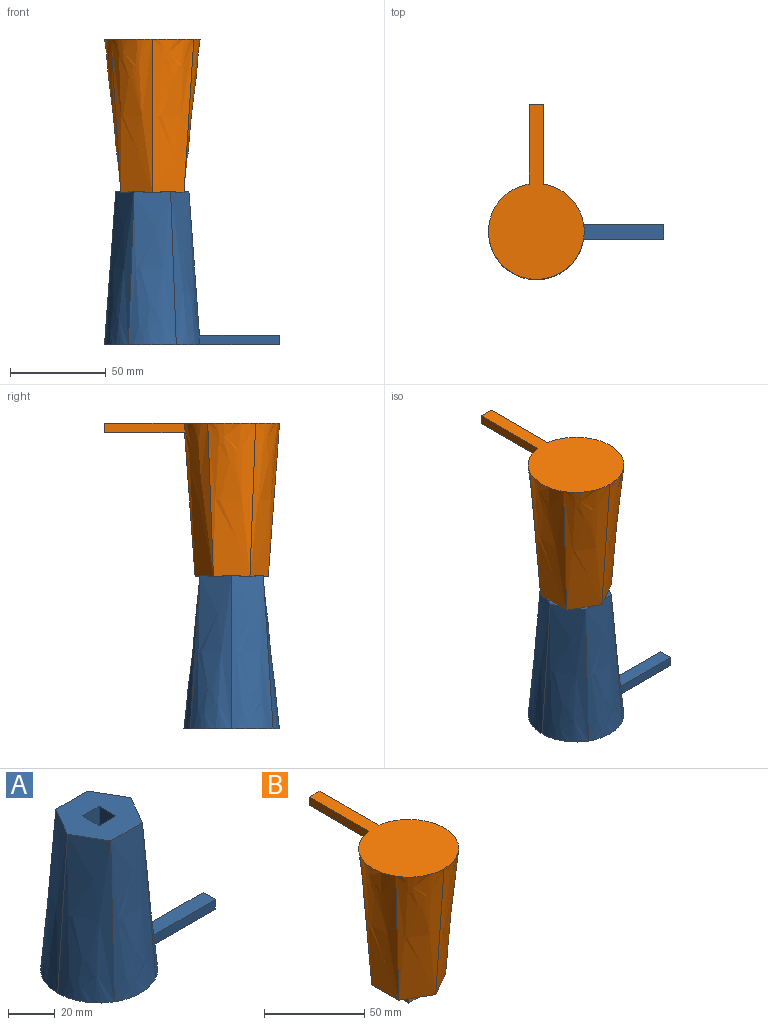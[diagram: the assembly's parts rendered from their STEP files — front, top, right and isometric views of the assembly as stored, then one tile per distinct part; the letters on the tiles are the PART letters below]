
ASSEMBLY  parts=2 mates=1
PART A: 19 faces, bbox 91.5x50x80 mm
  f0: bspline ~80x21.65mm, area 1787.3mm2, adj f1,f2,f6,f7,f16,f18
  f1: plane 91.45x50mm, normal (0,0,-1), area 1957.7mm2, adj f0,f3,f4,f5,f6,f7,f8,f15
  f2: plane 38.21x33.09mm, normal (0,0,1), area 846.4mm2, adj f0,f3,f4,f5,f6,f7,f10,f11
  f3: bspline ~80x25mm, area 1806mm2, adj f1,f2,f4,f7
  f4: bspline ~80x21.65mm, area 1806mm2, adj f1,f2,f3,f5
  f5: bspline ~80x21.65mm, area 1806mm2, adj f1,f2,f4,f6
  f6: bspline ~80x25mm, area 1806mm2, adj f0,f1,f2,f5
  f7: bspline ~80x21.65mm, area 1787.3mm2, adj f0,f1,f2,f3,f15,f18
  f8: cylinder r=10mm len=20mm, axis (0,0,-1), area 377mm2, adj f1,f9
  f9: plane 20x20mm, normal (0,0,-1), area 314.2mm2, adj f8
  f10: plane 10.1x10.1mm, normal (0,-1,0), area 102mm2, adj f2,f11,f13,f14
  f11: plane 10.1x10.1mm, normal (1,0,0), area 102mm2, adj f2,f10,f12,f14
  f12: plane 10.1x10.1mm, normal (0,1,0), area 102mm2, adj f2,f11,f13,f14
  f13: plane 10.1x10.1mm, normal (-1,0,0), area 102mm2, adj f2,f10,f12,f14
  f14: plane 10.1x10.1mm, normal (0,0,1), area 102mm2, adj f10,f11,f12,f13
  f15: plane 42.18x5mm, normal (0,1,0), area 209.8mm2, adj f1,f7,f17,f18
  f16: plane 42.18x5mm, normal (0,-1,0), area 209.8mm2, adj f0,f1,f17,f18
  f17: plane 7.42x5mm, normal (1,0,0), area 37.1mm2, adj f1,f15,f16,f18
  f18: plane 42.18x7.43mm, normal (0,0,1), area 311.4mm2, adj f0,f7,f15,f16,f17
PART B: 17 faces, bbox 50x91.5x89.8 mm
  f0: bspline ~80x21.65mm, area 1787.3mm2, adj f6,f7,f8,f9,f15,f16
  f1: plane 9.8x9.8mm, normal (0,-1,0), area 96mm2, adj f2,f4,f5,f6
  f2: plane 9.8x9.8mm, normal (1,0,0), area 96mm2, adj f1,f3,f5,f6
  f3: plane 9.8x9.8mm, normal (0,1,0), area 96mm2, adj f2,f4,f5,f6
  f4: plane 9.8x9.8mm, normal (-1,0,0), area 96mm2, adj f1,f3,f5,f6
  f5: plane 9.8x9.8mm, normal (0,0,-1), area 96mm2, adj f1,f2,f3,f4
  f6: plane 38.21x33.09mm, normal (0,0,-1), area 852.3mm2, adj f0,f1,f2,f3,f4,f8,f9,f10
  f7: plane 91.45x50mm, normal (0,0,1), area 2271.8mm2, adj f0,f8,f9,f10,f11,f12,f13,f14
  f8: bspline ~80x25mm, area 1806mm2, adj f0,f6,f7,f12
  f9: bspline ~80x21.65mm, area 1787.3mm2, adj f0,f6,f7,f10,f14,f16
  f10: bspline ~80x25mm, area 1806mm2, adj f6,f7,f9,f11
  f11: bspline ~80x21.65mm, area 1806mm2, adj f6,f7,f10,f12
  f12: bspline ~80x21.65mm, area 1806mm2, adj f6,f7,f8,f11
  f13: plane 7.42x5mm, normal (0,1,0), area 37.1mm2, adj f7,f14,f15,f16
  f14: plane 42.18x5mm, normal (-1,0,0), area 209.8mm2, adj f7,f9,f13,f16
  f15: plane 42.18x5mm, normal (1,0,0), area 209.8mm2, adj f0,f7,f13,f16
  f16: plane 42.18x7.43mm, normal (0,0,-1), area 311.4mm2, adj f0,f9,f13,f14,f15
PLACE A t=(15.88,42.86,-64.27)mm
PLACE B t=(15.88,42.86,5.63)mm
MATE fastened A.f8 <-> B.f5  axis (0,0,1) through (15.88,42.86,5.63)mm
